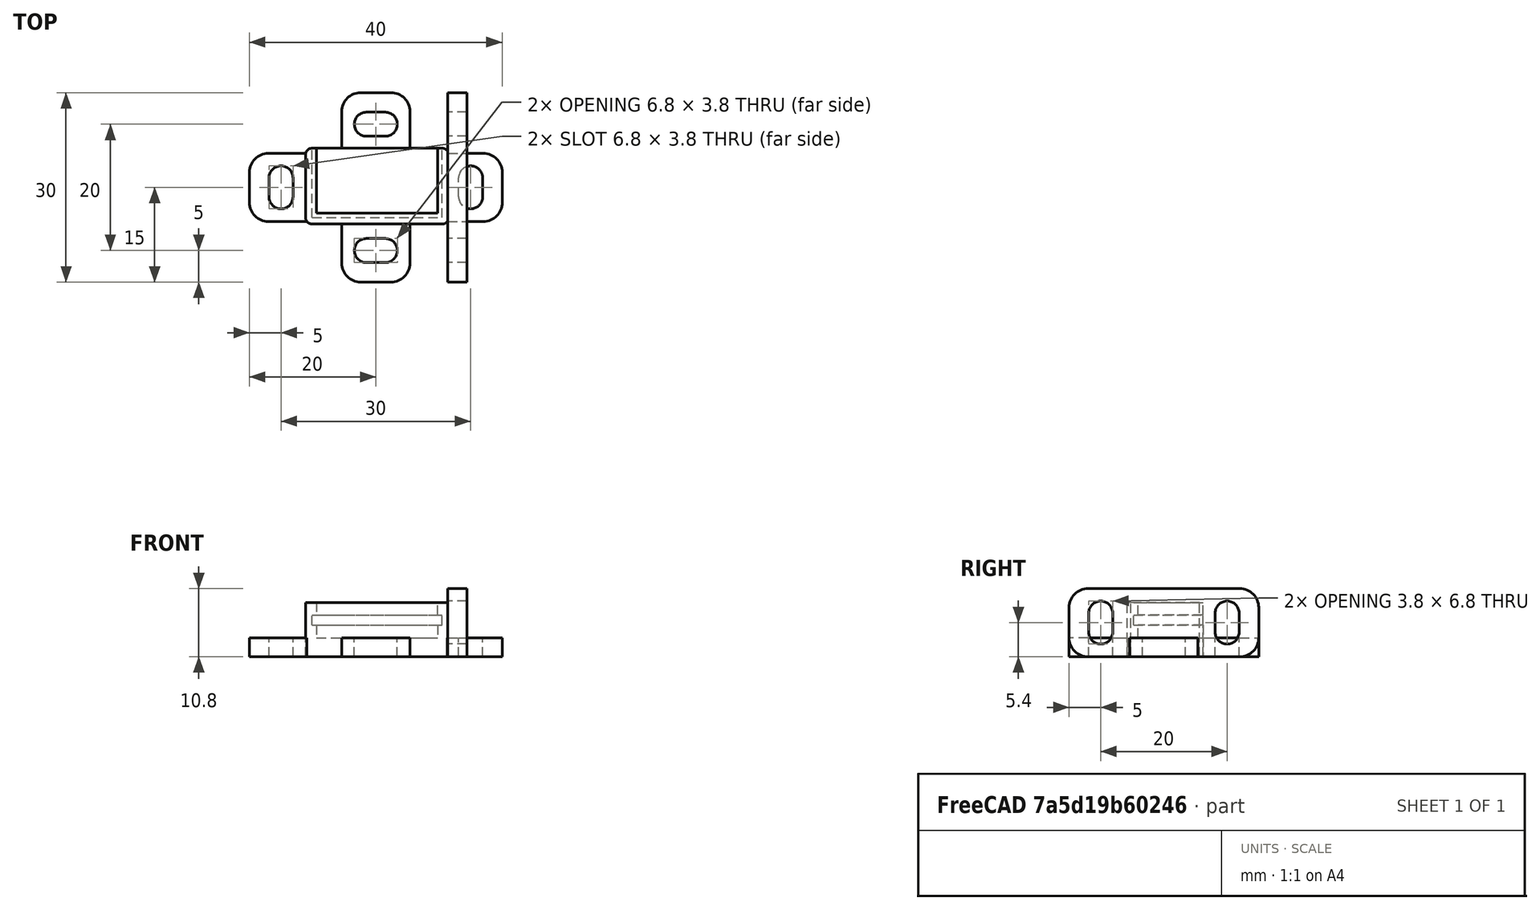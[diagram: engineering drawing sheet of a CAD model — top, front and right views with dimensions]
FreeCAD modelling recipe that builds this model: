
FCSTD DOCUMENT  (FreeCAD 0.19R)
Label: step_down_hw-613
License: FreeArt
LicenseURL: http://artlibre.org/licence/lal
objects: Part::Box×9, Part::MultiFuse×6, Part::Cut×4, App::Part×4, Part::Fillet×3, Part::Feature×3, Spreadsheet::Sheet×1
note: 25 computed .brp shape members not serialized (recipe doc carries the construction recipe); baked Part::Feature solids carry a one-line shape summary decoded from their .brp

FEATURE [Spreadsheet::Sheet] Spreadsheet  label="p"
  cells = A1=pcb_x; B1(pcb_x)=20.6; A2=pcb_y; B2(pcb_y)=11; A3=pcb_z; B3(pcb_z)=1.6; A4=pcb_under; B4(pcb_under)=2; A5=side_wall; B5(side_wall)=1; A6=pcb_side_lane; B6(pcb_side_lane)=0.7; A7=bottom_wall; B7(bottom_wall)=3; A8=pcb_above; B8(pcb_above)=2; A9=box_x; B9(box_x)==pcb_x + 2 * side_wall; A10=box_y; B10(box_y)==pcb_y + side_wall; A11=box_z; B11(box_z)==bottom_wall + pcb_under + pcb_z + pcb_above
FEATURE [Part::Box] Box  label="external cube"
  AttacherType = Attacher::AttachEngine3D
  Height = 8.6
  Length = 22.6
  Width = 12
  expr: Length = <<p>>.box_x
  expr: Width = <<p>>.box_y
  expr: Height = <<p>>.box_z
FEATURE [Part::Box] Box006  label="internal cube"
  AttacherType = Attacher::AttachEngine3D
  Height = 5.6
  Length = 19.2
  Placement = pos=(1.7,1.7,3) rot=(0,0,1;0rad)
  Width = 10.6
  expr: Length = <<p>>.pcb_x - 2 * <<p>>.pcb_side_lane
  expr: Width = <<p>>.pcb_y - 2 * <<p>>.pcb_side_lane + <<p>>.side_wall
  expr: Height = <<p>>.pcb_under + <<p>>.pcb_z + <<p>>.pcb_above
  expr: .Placement.Base.z = <<p>>.bottom_wall
  expr: .Placement.Base.x = <<p>>.side_wall + <<p>>.pcb_side_lane
  expr: .Placement.Base.y = <<p>>.side_wall + <<p>>.pcb_side_lane
FEATURE [Part::Box] Box007  label="pcb extract cube"
  AttacherType = Attacher::AttachEngine3D
  Height = 1.6
  Length = 20.6
  Placement = pos=(1,1,5) rot=(0,0,1;0rad)
  Width = 11
  expr: Height = <<p>>.pcb_z
  expr: .Placement.Base.z = <<p>>.bottom_wall + <<p>>.pcb_under
  expr: Width = <<p>>.pcb_y
  expr: Length = <<p>>.pcb_x
  expr: .Placement.Base.x = <<p>>.side_wall
  expr: .Placement.Base.y = <<p>>.side_wall
FEATURE [Part::MultiFuse] Fusion  label="extract fusion"
  Shapes = -> [Box006,Box007]
FEATURE [Part::Fillet] Fillet  label="external fillet"
  Base = -> Box
  Edges = 4 edges r=1: [Edge1,Edge3,Edge5,Edge7]
FEATURE [Part::Feature] Cut003002  label="attach plane x dir002"
  shape: bbox 40 x 10.8 x 3 mm, 18 faces (baked)
FEATURE [Part::MultiFuse] Fusion001  label="outer fusion"
  Shapes = -> [Fillet,Cut003002]
FEATURE [Part::Cut] Cut  label="hw-613 cut"
  Base = -> Fusion001
  Tool = -> Fusion
FEATURE [App::Part] Part  label="hw-613 pcb box part"
  Group = -> [Box006,Box007,Fusion,Cut]
  Origin = -> Origin
FEATURE [Part::Box] Box008  label="external cube001"
  AttacherType = Attacher::AttachEngine3D
  Height = 8.6
  Length = 22.6
  Width = 12
  expr: Length = <<p>>.box_x
  expr: Width = <<p>>.box_y
  expr: Height = <<p>>.box_z
FEATURE [Part::Fillet] Fillet001  label="external fillet001"
  Base = -> Box008
  Edges = 4 edges r=1: [Edge1,Edge3,Edge5,Edge7]
FEATURE [Part::Box] Box009  label="internal cube001"
  AttacherType = Attacher::AttachEngine3D
  Height = 5.6
  Length = 19.2
  Placement = pos=(1.7,1.7,3) rot=(0,0,1;0rad)
  Width = 10.6
  expr: Length = <<p>>.pcb_x - 2 * <<p>>.pcb_side_lane
  expr: Width = <<p>>.pcb_y - 2 * <<p>>.pcb_side_lane + <<p>>.side_wall
  expr: Height = <<p>>.pcb_under + <<p>>.pcb_z + <<p>>.pcb_above
  expr: .Placement.Base.z = <<p>>.bottom_wall
  expr: .Placement.Base.x = <<p>>.side_wall + <<p>>.pcb_side_lane
  expr: .Placement.Base.y = <<p>>.side_wall + <<p>>.pcb_side_lane
FEATURE [Part::Box] Box010  label="pcb extract cube001"
  AttacherType = Attacher::AttachEngine3D
  Height = 1.6
  Length = 20.6
  Placement = pos=(1,1,5) rot=(0,0,1;0rad)
  Width = 11
  expr: Height = <<p>>.pcb_z
  expr: .Placement.Base.z = <<p>>.bottom_wall + <<p>>.pcb_under
  expr: Width = <<p>>.pcb_y
  expr: Length = <<p>>.pcb_x
  expr: .Placement.Base.x = <<p>>.side_wall
  expr: .Placement.Base.y = <<p>>.side_wall
FEATURE [Part::MultiFuse] Fusion003  label="extract fusion001"
  Shapes = -> [Box009,Box010]
FEATURE [Part::Feature] Cut002001  label="attach plane y dir"
  shape: bbox 10.8 x 30 x 3 mm, 18 faces (baked)
FEATURE [Part::MultiFuse] Fusion002  label="outer fusion001"
  Shapes = -> [Fillet001,Cut002001]
FEATURE [Part::Cut] Cut003003  label="hw-613 cut y"
  Base = -> Fusion002
  Tool = -> Fusion003
FEATURE [App::Part] Part001  label="hw-613 pcb box y part"
  Group = -> [Fusion003,Box010,Fillet001,Box008,Fusion002,Box009,Cut002001,Cut003003]
  Origin = -> Origin001
FEATURE [Part::Box] Box011  label="external cube002"
  AttacherType = Attacher::AttachEngine3D
  Height = 8.6
  Length = 22.6
  Width = 12
  expr: Height = <<p>>.box_z
  expr: Width = <<p>>.box_y
  expr: Length = <<p>>.box_x
FEATURE [Part::Fillet] Fillet002  label="external fillet002"
  Base = -> Box011
  Edges = 4 edges r=1: [Edge1,Edge3,Edge5,Edge7]
FEATURE [Part::Box] Box012  label="internal cube002"
  AttacherType = Attacher::AttachEngine3D
  Height = 5.6
  Length = 19.2
  Placement = pos=(1.7,1.7,3) rot=(0,0,1;0rad)
  Width = 10.6
  expr: .Placement.Base.y = <<p>>.side_wall + <<p>>.pcb_side_lane
  expr: .Placement.Base.x = <<p>>.side_wall + <<p>>.pcb_side_lane
  expr: .Placement.Base.z = <<p>>.bottom_wall
  expr: Height = <<p>>.pcb_under + <<p>>.pcb_z + <<p>>.pcb_above
  expr: Width = <<p>>.pcb_y - 2 * <<p>>.pcb_side_lane + <<p>>.side_wall
  expr: Length = <<p>>.pcb_x - 2 * <<p>>.pcb_side_lane
FEATURE [Part::Box] Box013  label="pcb extract cube002"
  AttacherType = Attacher::AttachEngine3D
  Height = 1.6
  Length = 20.6
  Placement = pos=(1,1,5) rot=(0,0,1;0rad)
  Width = 11
  expr: .Placement.Base.y = <<p>>.side_wall
  expr: .Placement.Base.x = <<p>>.side_wall
  expr: Length = <<p>>.pcb_x
  expr: Width = <<p>>.pcb_y
  expr: .Placement.Base.z = <<p>>.bottom_wall + <<p>>.pcb_under
  expr: Height = <<p>>.pcb_z
FEATURE [Part::MultiFuse] Fusion005  label="extract fusion002"
  Shapes = -> [Box012,Box013]
FEATURE [Part::Feature] Cut003005  label="attach plane y dir001"
  Placement = pos=(25.5,0,-5.7) rot=(0,-1,0;1.5708rad)
  shape: bbox 3 x 30 x 10.8 mm, 18 faces (baked)
FEATURE [Part::MultiFuse] Fusion004  label="outer fusion002"
  Shapes = -> [Fillet002,Cut003005]
FEATURE [Part::Cut] Cut003004  label="hw-613 cut z"
  Base = -> Fusion004
  Tool = -> Fusion005
FEATURE [App::Part] Part002  label="hw-613 pcb box z part"
  Group = -> [Fusion005,Box013,Fillet002,Box011,Fusion004,Box012,Cut003005,Cut003004]
  Origin = -> Origin002
FEATURE [Part::Cut] Cut003006  label="hw-613 cut001"
  Base = -> Fillet
  Tool = -> Fusion
FEATURE [App::Part] Part003  label="hw-613 pcb box part no attach"
  Group = -> [Cut003006]
  Origin = -> Origin003
